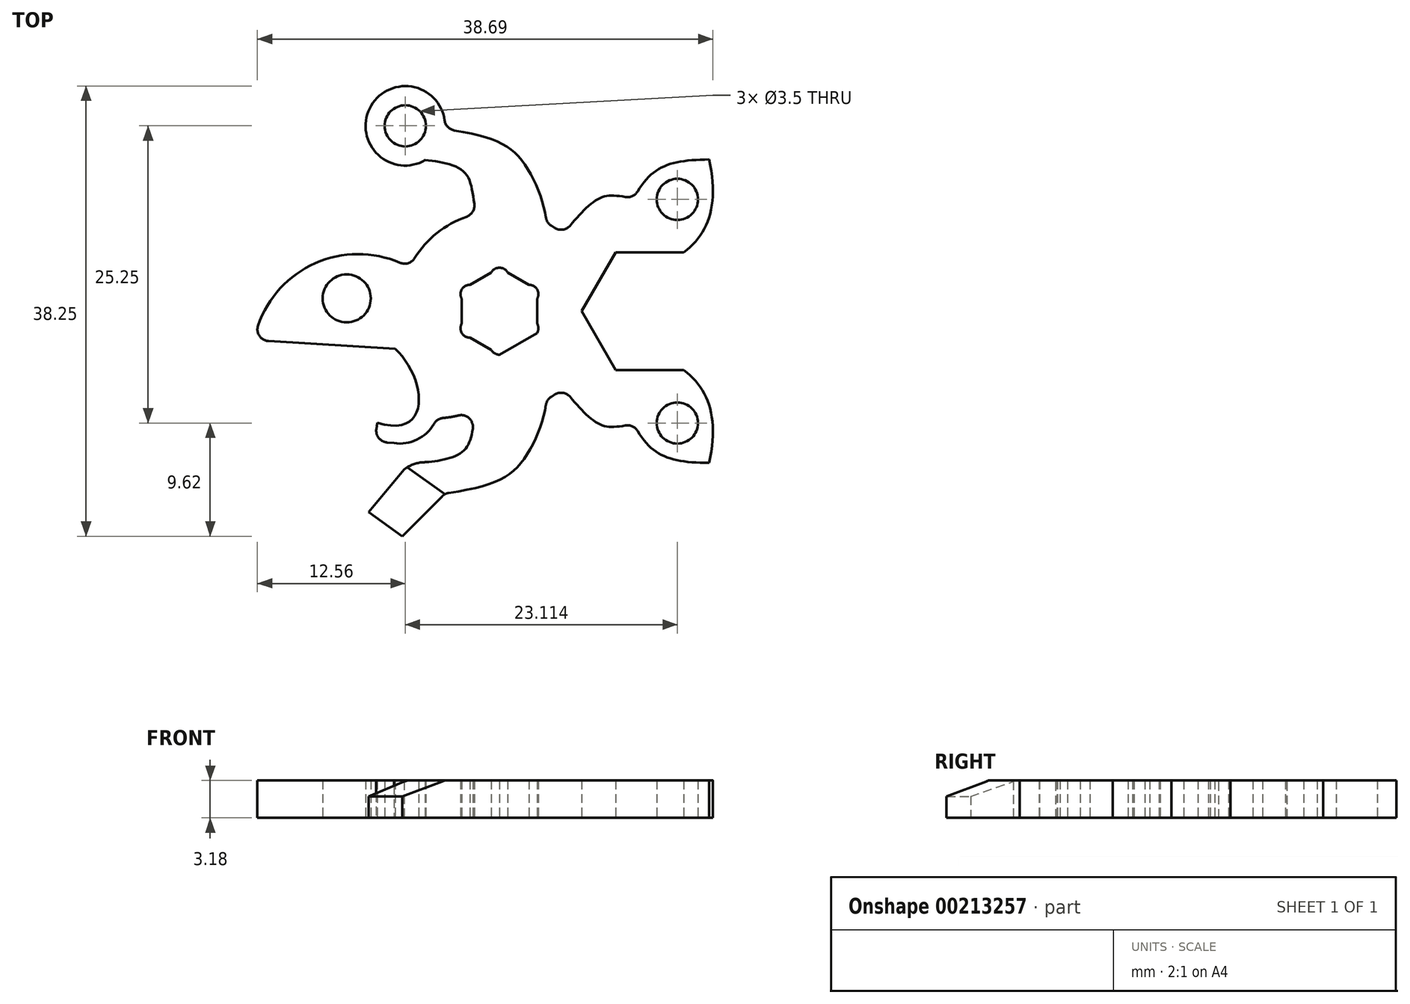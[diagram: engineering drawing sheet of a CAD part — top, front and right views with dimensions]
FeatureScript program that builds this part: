
annotation { "Feature Type Name" : "Feature", "Feature Type Description" : "" }
export const myFeature = defineFeature(function(context is Context, id is Id, definition is map)
    precondition{}
    {
        {
            var Q0;
            Q0=qCreatedBy(makeId("Top.planeOp"),FACE);
            var sketch = newSketch(context, id + "F0", { "sketchPlane" : qUnion([Q0])});
            skCircle(sketch, "E0.cCircle", {"center": v(0, 0) * mm, "radius": 3.2 * mm, "construction": true});
            skLineSegment(sketch, "E0.0", {"start": v(3.2, -1.85) * mm, "end": v(0, -3.7) * mm});
            skLineSegment(sketch, "E0.1", {"start": v(0, -3.7) * mm, "end": v(-3.2, -1.85) * mm});
            skLineSegment(sketch, "E0.2", {"start": v(-3.2, -1.85) * mm, "end": v(-3.2, 1.85) * mm});
            skLineSegment(sketch, "E0.3", {"start": v(-3.2, 1.85) * mm, "end": v(0, 3.7) * mm});
            skLineSegment(sketch, "E0.4", {"start": v(0, 3.7) * mm, "end": v(3.2, 1.85) * mm});
            skLineSegment(sketch, "E0.5", {"start": v(3.2, 1.85) * mm, "end": v(3.2, -1.85) * mm});
            skPoint(sketch, "E0.0.midPoint", {"position": v(1.6, -2.77) * mm});
            skLineSegment(sketch, "E1.1", {"start": v(15.65, -5) * mm, "end": v(9.88, -5) * mm});
            skLineSegment(sketch, "E1.2", {"start": v(9.88, -5) * mm, "end": v(6.99, 0) * mm});
            skLineSegment(sketch, "E1.3", {"start": v(6.99, 0) * mm, "end": v(9.88, 5) * mm});
            skLineSegment(sketch, "E1.4", {"start": v(9.88, 5) * mm, "end": v(15.65, 5) * mm});
            skCircle(sketch, "E2", {"center": v(15.11, 9.5) * mm, "radius": 1.75 * mm});
            skCircle(sketch, "E3", {"center": v(-8, 15.75) * mm, "radius": 1.75 * mm});
            skFitSpline(sketch, "E4", {"points": [v(15.65, 5) * mm, v(17.82, 12.9) * mm], "startDerivative": vector(6.47, 4.85) * mm, "endDerivative": vector(-2.47, 11.54) * mm});
            skFitSpline(sketch, "E5", {"points": [v(17.82, 12.9) * mm, v(11.4, 9.57) * mm], "startDerivative": vector(-9.97, -0.1) * mm, "endDerivative": vector(-4.1, -8.35) * mm});
            skCircle(sketch, "E6", {"center": v(0, 0) * mm, "radius": 8.5 * mm});
            skCircle(sketch, "E7", {"center": v(-12.97, 1.1) * mm, "radius": 2.04 * mm});
            skLineSegment(sketch, "E8", {"start": v(0, 0) * mm, "end": v(0, 0) * mm});
            skPoint(sketch, "E8.endSnap0", {"position": v(3.2, 0) * mm});
            skFitSpline(sketch, "E9", {"points": [v(11.4, 9.57) * mm, v(8.44, 9.57) * mm, v(5.38, 6.58) * mm], "startDerivative": vector(-8.89, 1.7) * mm, "endDerivative": vector(-5.95, -6.5) * mm});
            skCircle(sketch, "E10", {"center": v(-8, 15.75) * mm, "radius": 3.38 * mm});
            skFitSpline(sketch, "E11", {"points": [v(4, 7.5) * mm, v(2, 12.7) * mm, v(-4.64, 15.49) * mm], "startDerivative": vector(-0.87, 10.23) * mm, "endDerivative": vector(-21.72, 3.2) * mm});
            skLineSegment(sketch, "E12", {"start": v(0, -23.93) * mm, "end": v(0, 25.87) * mm, "construction": true});
            skFitSpline(sketch, "E13", {"points": [v(-2, 8.26) * mm, v(-3, 11.8) * mm, v(-6.3, 12.83) * mm], "startDerivative": vector(-1.8, 9.62) * mm, "endDerivative": vector(-7.26, 0.59) * mm});
            skFitSpline(sketch, "E14.MirrorCS", {"points": [v(15.65, -5) * mm, v(17.82, -12.9) * mm], "startDerivative": vector(6.47, -4.85) * mm, "endDerivative": vector(-2.47, -11.54) * mm});
            skFitSpline(sketch, "E15.MirrorCS", {"points": [v(17.82, -12.9) * mm, v(11.4, -9.57) * mm], "startDerivative": vector(-9.97, 0.1) * mm, "endDerivative": vector(-4.1, 8.35) * mm});
            skCircle(sketch, "E16.MirrorC", {"center": v(15.11, -9.5) * mm, "radius": 1.75 * mm});
            skFitSpline(sketch, "E17.MirrorCS", {"points": [v(11.4, -9.57) * mm, v(8.44, -9.57) * mm, v(5.38, -6.58) * mm], "startDerivative": vector(-8.89, -1.7) * mm, "endDerivative": vector(-5.95, 6.5) * mm});
            skFitSpline(sketch, "E18.MirrorCS", {"points": [v(4, -7.5) * mm, v(2, -12.7) * mm, v(-4.64, -15.49) * mm], "startDerivative": vector(-0.87, -10.23) * mm, "endDerivative": vector(-21.72, -3.2) * mm});
            skFitSpline(sketch, "E19.MirrorCS", {"points": [v(-2, -8.26) * mm, v(-3, -11.8) * mm, v(-6.3, -12.83) * mm], "startDerivative": vector(-1.8, -9.62) * mm, "endDerivative": vector(-7.26, -0.59) * mm});
            skCircle(sketch, "E20", {"center": v(-12, -4.15) * mm, "radius": 9 * mm});
            skFitSpline(sketch, "E21", {"points": [v(-8.87, -3.2) * mm, v(-10.38, -9.46) * mm], "startDerivative": vector(7.48, -6.49) * mm, "endDerivative": vector(-14.73, 4.56) * mm});
            skLineSegment(sketch, "E22", {"start": v(-11.11, -17.06) * mm, "end": v(-8.26, -19.12) * mm});
            skLineSegment(sketch, "E23", {"start": v(-11.11, -17.06) * mm, "end": v(-8.08, -13.44) * mm});
            skLineSegment(sketch, "E24", {"start": v(-8.26, -19.12) * mm, "end": v(-4.64, -15.49) * mm});
            skLineSegment(sketch, "E25", {"start": v(-20.84, -2.46) * mm, "end": v(-8.87, -3.2) * mm});
            skLineSegment(sketch, "E26", {"start": v(-10.38, -9.46) * mm, "end": v(-10.6, -11.05) * mm});
            skLineSegment(sketch, "E27", {"start": v(-10.6, -11.05) * mm, "end": v(-8.96, -11.2) * mm});
            skArc(sketch, "E28", {"start": v(-5.34, -9.08) * mm, "mid": v(-3.62, -8.89) * mm, "end": v(-2, -8.26) * mm});
            skArc(sketch, "E29", {"start": v(-8.96, -11.2) * mm, "mid": v(-6.77, -10.79) * mm, "end": v(-5.34, -9.08) * mm});
            skCircle(sketch, "E30", {"center": v(0, 2.9) * mm, "radius": 0.8 * mm});
            skLineSegment(sketch, "E31", {"start": v(-3.2, 1.85) * mm, "end": v(3.2, -1.85) * mm, "construction": true});
            skLineSegment(sketch, "E32", {"start": v(3.2, 1.85) * mm, "end": v(-3.2, -1.85) * mm, "construction": true});
            skCircle(sketch, "E33", {"center": v(2.5, 1.45) * mm, "radius": 0.8 * mm});
            skCircle(sketch, "E34", {"center": v(2.5, -1.45) * mm, "radius": 0.8 * mm});
            skCircle(sketch, "E35", {"center": v(-2.5, -1.45) * mm, "radius": 0.8 * mm});
            skCircle(sketch, "E36", {"center": v(-2.5, 1.45) * mm, "radius": 0.8 * mm});
            skCircle(sketch, "E37", {"center": v(0, -2.9) * mm, "radius": 0.8 * mm});
            skArc(sketch, "E38", {"start": v(-6.3, -12.83) * mm, "mid": v(-7.25, -12.98) * mm, "end": v(-8.08, -13.44) * mm});
            skSolve(sketch);
        }
        {
            var Q0;
            Q0=makeQuery(id+"F0.imprint","IMPRINT",FACE,{"disambiguationData":[TD([[makeQuery(id+"F0.imprint","IMPRINT",EDGE,{"derivedFrom":sQuery(id+"F0.wireOp",EDGE,"E0.0")}),1.0]])]});
            var Q1;
            {var subQ0=sQuery(id+"F0.wireOp",EDGE,"E11");Q1=makeQuery(id+"F0.imprint","IMPRINT",FACE,{"disambiguationData":[TD([[makeQuery(id+"F0.imprint","IMPRINT",EDGE,{"derivedFrom":subQ0}),1.0]])]});}
            var Q2;
            {var subQ4=sQuery(id+"F0.wireOp",EDGE,"E1.4");Q2=makeQuery(id+"F0.imprint","IMPRINT",FACE,{"disambiguationData":[TD([[makeQuery(id+"F0.imprint","IMPRINT",EDGE,{"derivedFrom":subQ4}),1.0]])]});}
            var Q3;
            Q3=makeQuery(id+"F0.imprint","IMPRINT",FACE,{"disambiguationData":[TD([[makeQuery(id+"F0.imprint","IMPRINT",EDGE,{"derivedFrom":sQuery(id+"F0.wireOp",EDGE,"E3")}),-1.0]])]});
            var Q4;
            {var subQ4=sQuery(id+"F0.wireOp",EDGE,"E1.1");Q4=makeQuery(id+"F0.imprint","IMPRINT",FACE,{"disambiguationData":[TD([[makeQuery(id+"F0.imprint","IMPRINT",EDGE,{"derivedFrom":subQ4}),1.0]])]});}
            var Q5;
            {var subQ0=sQuery(id+"F0.wireOp",EDGE,"E18.MirrorCS");Q5=makeQuery(id+"F0.imprint","IMPRINT",FACE,{"disambiguationData":[TD([[makeQuery(id+"F0.imprint","IMPRINT",EDGE,{"derivedFrom":subQ0}),-1.0]])]});}
            var Q6;
            Q6=makeQuery(id+"F0.imprint","IMPRINT",FACE,{"disambiguationData":[TD([[makeQuery(id+"F0.imprint","IMPRINT",EDGE,{"derivedFrom":sQuery(id+"F0.wireOp",EDGE,"696f2640-bdc8-43ef-9c82-46a867db36190.MirrorC")}),1.0]])]});
            var Q7;
            Q7=makeQuery(id+"F0.imprint","IMPRINT",FACE,{"disambiguationData":[TD([[makeQuery(id+"F0.imprint","IMPRINT",EDGE,{"derivedFrom":sQuery(id+"F0.wireOp",EDGE,"E7")}),-1.0]])]});
            var Q8;
            {var subQ0=sQuery(id+"F0.wireOp",EDGE,"E20");var subQ1=sQuery(id+"F0.wireOp",EDGE,"E6");var subQ2=makeQuery(id+"F0.imprint","INTERSECT",VERTEX,{"disambiguationData":[OD(0.0)],"derivedFrom":[subQ1,subQ0]});Q8=makeQuery(id+"F0.imprint","IMPRINT",FACE,{"disambiguationData":[TD([[makeQuery(id+"F0.imprint","IMPRINT",EDGE,{"disambiguationData":[TD([[subQ2,-1.0]])],"derivedFrom":subQ1}),1.0]])]});}
            var Q9;
            Q9=makeQuery(id+"F0.imprint","IMPRINT",FACE,{"disambiguationData":[TD([[makeQuery(id+"F0.imprint","IMPRINT",EDGE,{"derivedFrom":sQuery(id+"F0.wireOp",EDGE,"E22")}),1.0]])]});
            var Q10;
            {var subQ0=sQuery(id+"F0.wireOp",EDGE,"E26");Q10=makeQuery(id+"F0.imprint","IMPRINT",FACE,{"disambiguationData":[TD([[makeQuery(id+"F0.imprint","IMPRINT",EDGE,{"derivedFrom":subQ0}),1.0]])]});}
            var Q11;
            {var subQ0=sQuery(id+"F0.wireOp",EDGE,"kHHl4p63-yTGS-qJbq-Rno6-EFwizW5EomBi");Q11=makeQuery(id+"F0.imprint","IMPRINT",FACE,{"disambiguationData":[TD([[makeQuery(id+"F0.imprint","IMPRINT",EDGE,{"derivedFrom":subQ0}),1.0]])]});}
            var Q12;
            {var subQ0=sQuery(id+"F0.wireOp",EDGE,"WEDVExDZ-VBpb-CEiS-lfxq-Eqhz5oAIDfzZ");var subQ1=sQuery(id+"F0.wireOp",EDGE,"E6");var subQ2=makeQuery(id+"F0.imprint","INTERSECT",VERTEX,{"derivedFrom":[subQ1,subQ0]});Q12=makeQuery(id+"F0.imprint","IMPRINT",FACE,{"disambiguationData":[TD([[makeQuery(id+"F0.imprint","IMPRINT",EDGE,{"disambiguationData":[TD([[subQ2,1.0]])],"derivedFrom":subQ1}),-1.0]])]});}
            var Q13;
            {var subQ0=sQuery(id+"F0.wireOp",EDGE,"kc9krFET-Q98u-1ty7-TEbK-eGsMNFeJvKYa");Q13=makeQuery(id+"F0.imprint","IMPRINT",FACE,{"disambiguationData":[TD([[makeQuery(id+"F0.imprint","IMPRINT",EDGE,{"derivedFrom":subQ0}),1.0]])]});}
            var Q14;
            {var subQ0=sQuery(id+"F0.wireOp",EDGE,"E28");Q14=makeQuery(id+"F0.imprint","IMPRINT",FACE,{"disambiguationData":[TD([[makeQuery(id+"F0.imprint","IMPRINT",EDGE,{"derivedFrom":subQ0}),1.0]])]});}
            var Q15;
            {var subQ38=sQuery(id+"F0.wireOp",EDGE,"E34");var subQ39=sQuery(id+"F0.wireOp",EDGE,"E0.0");var subQ40=makeQuery(id+"F0.imprint","INTERSECT",VERTEX,{"derivedFrom":[subQ39,subQ38]});Q15=makeQuery(id+"F0.imprint","IMPRINT",FACE,{"disambiguationData":[TD([[makeQuery(id+"F0.imprint","IMPRINT",EDGE,{"disambiguationData":[TD([[subQ40,-1.0]])],"derivedFrom":subQ39}),1.0]])]});}
            extrude(context, id + "F1", {"entities" : qUnion([Q0, Q1, Q2, Q3, Q4, Q5, Q6, Q7, Q8, Q9, Q10, Q11, Q12, Q13, Q14, Q15]), "depth" : (.125 * 25.4) * mm});
        }
        {
            var Q0;
            Q0=makeQuery(id+"F1.opExtrude","SWEPT_EDGE",EDGE,{"disambiguationData":[OSD([sQuery(id+"F0.wireOp",EDGE,"E20"),sQuery(id+"F0.wireOp",EDGE,"E25")])]});
            var Q1;
            Q1=makeQuery(id+"F1.opExtrude","SWEPT_EDGE",EDGE,{"disambiguationData":[OSD([sQuery(id+"F0.wireOp",EDGE,"E6"),sQuery(id+"F0.wireOp",EDGE,"E20")])]});
            var Q2;
            Q2=makeQuery(id+"F1.opExtrude","SWEPT_EDGE",EDGE,{"disambiguationData":[OSD([sQuery(id+"F0.wireOp",EDGE,"E28"),sQuery(id+"F0.wireOp",EDGE,"E29")])]});
            var Q3;
            Q3=makeQuery(id+"F1.opExtrude","SWEPT_EDGE",EDGE,{"disambiguationData":[OSD([sQuery(id+"F0.wireOp",EDGE,"E6"),sQuery(id+"F0.wireOp",EDGE,"E19.MirrorCS"),sQuery(id+"F0.wireOp",EDGE,"E28")])]});
            var Q4;
            Q4=makeQuery(id+"F1.opExtrude","SWEPT_EDGE",EDGE,{"disambiguationData":[OSD([sQuery(id+"F0.wireOp",EDGE,"E6"),sQuery(id+"F0.wireOp",EDGE,"E18.MirrorCS")])]});
            var Q5;
            Q5=makeQuery(id+"F1.opExtrude","SWEPT_EDGE",EDGE,{"disambiguationData":[OSD([sQuery(id+"F0.wireOp",EDGE,"E6"),sQuery(id+"F0.wireOp",EDGE,"E17.MirrorCS")])]});
            var Q6;
            Q6=makeQuery(id+"F1.opExtrude","SWEPT_EDGE",EDGE,{"disambiguationData":[OSD([sQuery(id+"F0.wireOp",EDGE,"E6"),sQuery(id+"F0.wireOp",EDGE,"E9")])]});
            var Q7;
            Q7=makeQuery(id+"F1.opExtrude","SWEPT_EDGE",EDGE,{"disambiguationData":[OSD([sQuery(id+"F0.wireOp",EDGE,"E6"),sQuery(id+"F0.wireOp",EDGE,"E11")])]});
            var Q8;
            Q8=makeQuery(id+"F1.opExtrude","SWEPT_EDGE",EDGE,{"disambiguationData":[OSD([sQuery(id+"F0.wireOp",EDGE,"E6"),sQuery(id+"F0.wireOp",EDGE,"E13")])]});
            var Q9;
            Q9=makeQuery(id+"F1.opExtrude","SWEPT_EDGE",EDGE,{"disambiguationData":[OSD([sQuery(id+"F0.wireOp",EDGE,"E10"),sQuery(id+"F0.wireOp",EDGE,"E11")])]});
            var Q10;
            Q10=makeQuery(id+"F1.opExtrude","SWEPT_EDGE",EDGE,{"disambiguationData":[OSD([sQuery(id+"F0.wireOp",EDGE,"E5"),sQuery(id+"F0.wireOp",EDGE,"E9")])]});
            var Q11;
            Q11=makeQuery(id+"F1.opExtrude","SWEPT_EDGE",EDGE,{"disambiguationData":[OSD([sQuery(id+"F0.wireOp",EDGE,"E18.MirrorCS"),sQuery(id+"F0.wireOp",EDGE,"f574427c-449b-4b5e-b643-932bfef207600.MirrorC")])]});
            var Q12;
            Q12=makeQuery(id+"F1.opExtrude","SWEPT_EDGE",EDGE,{"disambiguationData":[OSD([sQuery(id+"F0.wireOp",EDGE,"E19.MirrorCS"),sQuery(id+"F0.wireOp",EDGE,"f574427c-449b-4b5e-b643-932bfef207600.MirrorC")])]});
            var Q13;
            Q13=makeQuery(id+"F1.opExtrude","SWEPT_EDGE",EDGE,{"disambiguationData":[OSD([sQuery(id+"F0.wireOp",EDGE,"E26"),sQuery(id+"F0.wireOp",EDGE,"E27")])]});
            var Q14;
            Q14=makeQuery(id+"F1.opExtrude","SWEPT_EDGE",EDGE,{"disambiguationData":[OSD([sQuery(id+"F0.wireOp",EDGE,"E15.MirrorCS"),sQuery(id+"F0.wireOp",EDGE,"E17.MirrorCS")])]});
            fillet(context, id + "F2", {"entities" : qUnion([Q0, Q1, Q2, Q3, Q4, Q5, Q6, Q7, Q8, Q9, Q10, Q11, Q12, Q13, Q14]), "radius" : 1 * mm, "tangentPropagation" : true, "allowEdgeOverflow" : false});
        }
        {
            var Q0;
            Q0=makeQuery(id+"F1.opExtrude","CAP_EDGE",EDGE,{"disambiguationData":[OSD([sQuery(id+"F0.wireOp",EDGE,"E22")])],"isStart":false});
            chamfer(context, id + "F3", {"entities" : qUnion([Q0]), "chamferType" : ChamferType.OFFSET_ANGLE, "width" : 5 * mm, "oppositeDirection" : false, "angle" : 15 * degree, "tangentPropagation" : true});
        }
    });
